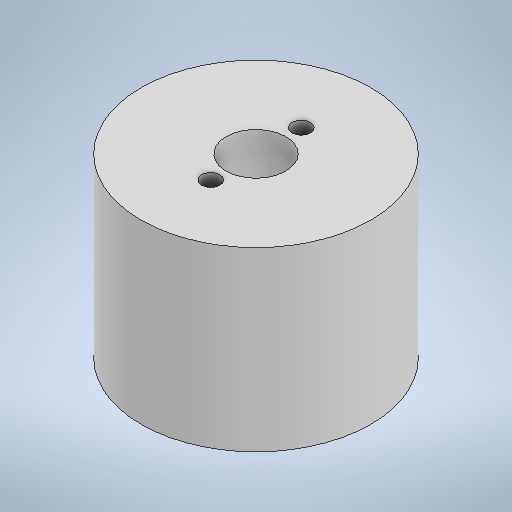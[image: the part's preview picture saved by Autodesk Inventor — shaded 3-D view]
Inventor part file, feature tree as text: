
AUTODESK INVENTOR PART (.ipt)
format: ipt  version: 2025.2 (Build 292293000, 293)  size: 221,184 bytes
history: native  units: in
note: dims shown in document units (in); Inventor stores cm internally (conversion verified against a paired STEP export)
features: extrude x3, sketch x3
ambient origin geometry x8: Origin, YZ Plane, XZ Plane, XY Plane, X Axis, Y Axis, Z Axis, Center Point
bodies: Solid1 (feature_tree)
feature tree (6):
  extrude  "Extrusion1"  Depth=0.26in
  extrude  "Extrusion2"  Depth=0.197in
  extrude  "Extrusion3"  Depth=0.197in
  sketch  "Sketch1"  dims[d0=1.0in d1=0.26in]
  sketch  "Sketch2"  dims[d2=0.7706in d3=0.0in d4=0.197in]
  sketch  "Sketch3"  dims[d5=0.197in d6=0.0797in d7=0.0797in d8=0.175in d9=0.0in d10=0.197in d12=0.175in d13=0.0in d15=0.0797in d16=0.197in d17=0.0797in]
